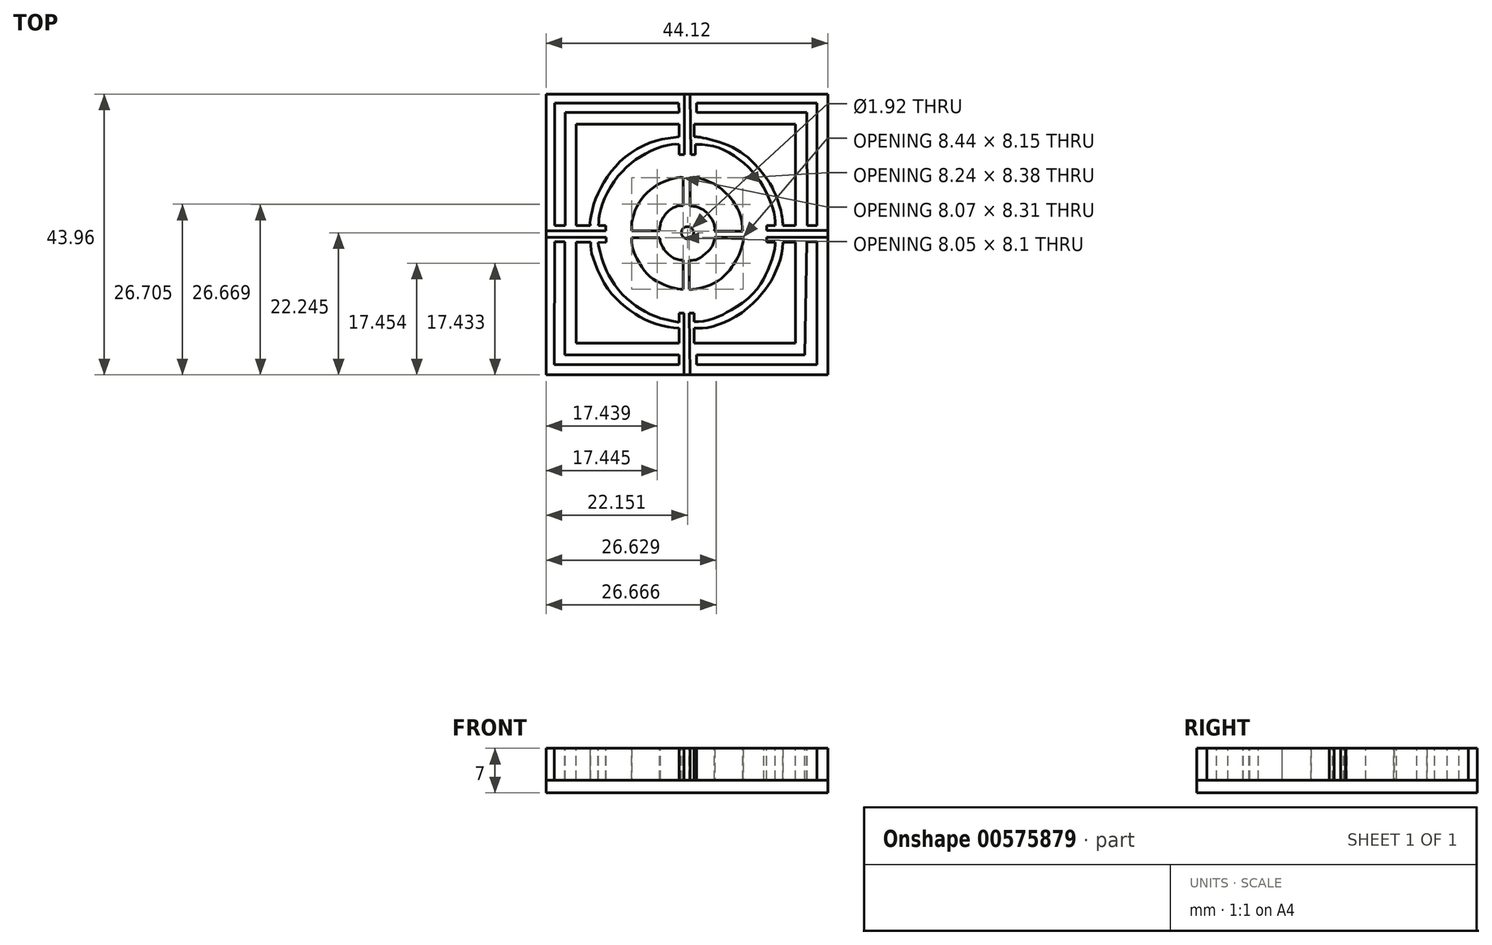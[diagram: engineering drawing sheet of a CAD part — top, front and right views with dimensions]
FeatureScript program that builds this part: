
annotation { "Feature Type Name" : "Feature", "Feature Type Description" : "" }
export const myFeature = defineFeature(function(context is Context, id is Id, definition is map)
    precondition{}
    {
        {
            var Q0;
            Q0=qCreatedBy(makeId("Top.planeOp"),FACE);
            var sketch = newSketch(context, id + "F0", { "sketchPlane" : qUnion([Q0])});
            skFitSpline(sketch, "E0", {"points": [v(14.8, 62.13) * mm, v(14.75, 42.86) * mm], "startDerivative": vector(-0.06, -19.27) * mm, "endDerivative": vector(-0.06, -19.27) * mm});
            skFitSpline(sketch, "E1", {"points": [v(14.75, 42.86) * mm, v(34.31, 42.86) * mm], "startDerivative": vector(19.6, 0) * mm, "endDerivative": vector(19.6, 0) * mm});
            skFitSpline(sketch, "E2", {"points": [v(34.31, 42.86) * mm, v(34.31, 44.38) * mm], "startDerivative": vector(0, 1.53) * mm, "endDerivative": vector(0, 1.53) * mm});
            skFitSpline(sketch, "E3", {"points": [v(34.31, 44.38) * mm, v(16.42, 44.38) * mm], "startDerivative": vector(-17.93, 0) * mm, "endDerivative": vector(-17.93, 0) * mm});
            skFitSpline(sketch, "E4", {"points": [v(16.42, 44.38) * mm, v(16.42, 62.13) * mm], "startDerivative": vector(0, 17.74) * mm, "endDerivative": vector(0, 17.74) * mm});
            skFitSpline(sketch, "E5", {"points": [v(16.42, 62.13) * mm, v(14.8, 62.13) * mm], "startDerivative": vector(-1.62, 0) * mm, "endDerivative": vector(-1.62, 0) * mm});
            skFitSpline(sketch, "E6", {"points": [v(34.31, 50.95) * mm, v(34.31, 46.2) * mm], "startDerivative": vector(0, -4.75) * mm, "endDerivative": vector(0, -4.75) * mm});
            skFitSpline(sketch, "E7", {"points": [v(34.31, 50.95) * mm, v(36.65, 50.95) * mm], "startDerivative": vector(2.34, 0) * mm, "endDerivative": vector(2.34, 0) * mm});
            skFitSpline(sketch, "E8", {"points": [v(36.65, 50.95) * mm, v(36.65, 46.2) * mm], "startDerivative": vector(0, -4.75) * mm, "endDerivative": vector(0, -4.75) * mm});
            skFitSpline(sketch, "E9", {"points": [v(34.31, 49.46) * mm, v(33.12, 49.7) * mm, v(30.97, 50.3) * mm, v(28.74, 51.3) * mm, v(26.75, 52.67) * mm, v(24.79, 54.57) * mm, v(23.3, 56.84) * mm, v(22.67, 58.18) * mm, v(22.03, 60.1) * mm, v(21.6, 62) * mm, v(21.6, 62.01) * mm], "startDerivative": vector(-13.94, 2.4) * mm, "endDerivative": vector(0.26, 5.24) * mm});
            skFitSpline(sketch, "E10", {"points": [v(36.65, 48.6) * mm, v(38.29, 48.6) * mm, v(41.1, 49.37) * mm, v(44.58, 51.33) * mm, v(47.54, 54.27) * mm, v(48.82, 56.2) * mm, v(50.1, 59.12) * mm, v(50.59, 62.01) * mm], "startDerivative": vector(14.49, -1.02) * mm, "endDerivative": vector(1.9, 21.32) * mm});
            skFitSpline(sketch, "E11", {"points": [v(50.59, 62.01) * mm, v(49.36, 62.01) * mm], "startDerivative": vector(-1.25, 0) * mm, "endDerivative": vector(-1.25, 0) * mm});
            skFitSpline(sketch, "E12", {"points": [v(49.36, 62.01) * mm, v(49.36, 61.46) * mm, v(48.89, 59.4) * mm, v(47.94, 57.1) * mm, v(46.93, 55.26) * mm, v(44.59, 52.79) * mm, v(41.9, 51.12) * mm, v(40.57, 50.4) * mm, v(38.37, 49.72) * mm, v(36.65, 49.61) * mm], "startDerivative": vector(0.7, -10.36) * mm, "endDerivative": vector(-15.94, 0) * mm});
            skFitSpline(sketch, "E13", {"points": [v(50.59, 64.63) * mm, v(50.2, 67.1) * mm, v(48.89, 70.6) * mm, v(47.55, 72.58) * mm], "startDerivative": vector(-0.92, 7.67) * mm, "endDerivative": vector(-5.43, 6.35) * mm});
            skFitSpline(sketch, "E14", {"points": [v(47.55, 72.58) * mm, v(46.33, 74.1) * mm, v(42.46, 77) * mm, v(37.58, 78.46) * mm, v(36.87, 78.55) * mm], "startDerivative": vector(-4.95, 6.76) * mm, "endDerivative": vector(-4.27, 0.3) * mm});
            skFitSpline(sketch, "E15", {"points": [v(36.87, 78.55) * mm, v(36.87, 77.33) * mm], "startDerivative": vector(0, -1.08) * mm, "endDerivative": vector(0, -1.08) * mm});
            skFitSpline(sketch, "E16", {"points": [v(36.87, 77.33) * mm, v(37.6, 77.33) * mm, v(39.73, 77.05) * mm, v(42.02, 76.13) * mm, v(44.29, 74.55) * mm, v(46.26, 72.58) * mm, v(47.74, 70.32) * mm, v(48.72, 68.07) * mm, v(49.31, 66.05) * mm, v(49.38, 64.63) * mm], "startDerivative": vector(9.67, 0.58) * mm, "endDerivative": vector(-0.3, -15.03) * mm});
            skFitSpline(sketch, "E17", {"points": [v(49.38, 64.63) * mm, v(50.59, 64.63) * mm], "startDerivative": vector(1.24, 0) * mm, "endDerivative": vector(1.24, 0) * mm});
            skFitSpline(sketch, "E18", {"points": [v(34.3, 77.33) * mm, v(32.9, 77.33) * mm, v(29.97, 76.37) * mm, v(27.17, 74.7) * mm, v(24.52, 72.11) * mm, v(22.5, 68.62) * mm, v(21.8, 66.05) * mm, v(21.69, 64.63) * mm], "startDerivative": vector(-12.77, 1.45) * mm, "endDerivative": vector(-0.42, -12.91) * mm});
            skFitSpline(sketch, "E19", {"points": [v(21.69, 64.63) * mm, v(20.38, 64.63) * mm], "startDerivative": vector(-1.3, 0) * mm, "endDerivative": vector(-1.3, 0) * mm});
            skFitSpline(sketch, "E20", {"points": [v(20.38, 64.63) * mm, v(20.38, 65.43) * mm, v(21.02, 68.16) * mm, v(22.78, 71.84) * mm, v(25.97, 75.45) * mm, v(30.6, 77.89) * mm, v(34.3, 78.55) * mm], "startDerivative": vector(-0.6, 8.43) * mm, "endDerivative": vector(20.4, 2.18) * mm});
            skFitSpline(sketch, "E21", {"points": [v(34.3, 78.55) * mm, v(34.3, 77.33) * mm], "startDerivative": vector(0, -1.08) * mm, "endDerivative": vector(0, -1.08) * mm});
            skFitSpline(sketch, "E22", {"points": [v(22.84, 63.83) * mm, v(22.86, 62.77) * mm], "startDerivative": vector(0.02, -1.07) * mm, "endDerivative": vector(0.02, -1.07) * mm});
            skFitSpline(sketch, "E23", {"points": [v(22.86, 62.77) * mm, v(13.46, 62.77) * mm], "startDerivative": vector(-9.4, 0) * mm, "endDerivative": vector(-9.4, 0) * mm});
            skFitSpline(sketch, "E24", {"points": [v(13.46, 62.77) * mm, v(13.46, 63.83) * mm], "startDerivative": vector(0, 1.07) * mm, "endDerivative": vector(0, 1.07) * mm});
            skFitSpline(sketch, "E25", {"points": [v(13.46, 63.83) * mm, v(22.84, 63.83) * mm], "startDerivative": vector(9.38, 0) * mm, "endDerivative": vector(9.38, 0) * mm});
            skFitSpline(sketch, "E26", {"points": [v(34.93, 52.6) * mm, v(35.87, 52.6) * mm], "startDerivative": vector(0.94, 0) * mm, "endDerivative": vector(0.94, 0) * mm});
            skFitSpline(sketch, "E27", {"points": [v(35.87, 52.6) * mm, v(35.87, 59.23) * mm], "startDerivative": vector(-0.02, 6.18) * mm, "endDerivative": vector(0, 6.62) * mm});
            skFitSpline(sketch, "E28", {"points": [v(34.93, 52.6) * mm, v(34.93, 59.23) * mm], "startDerivative": vector(0, 6.62) * mm, "endDerivative": vector(0, 6.62) * mm});
            skFitSpline(sketch, "E29", {"points": [v(31.17, 62.76) * mm, v(24.72, 62.76) * mm], "startDerivative": vector(-6.45, 0) * mm, "endDerivative": vector(-6.45, 0) * mm});
            skFitSpline(sketch, "E30", {"points": [v(24.72, 62.76) * mm, v(24.72, 63.83) * mm], "startDerivative": vector(0, 1.07) * mm, "endDerivative": vector(0, 1.07) * mm});
            skFitSpline(sketch, "E31", {"points": [v(24.72, 63.83) * mm, v(31.17, 63.83) * mm], "startDerivative": vector(6.45, 0) * mm, "endDerivative": vector(6.45, 0) * mm});
            skFitSpline(sketch, "E32", {"points": [v(34.94, 67.78) * mm, v(34.94, 74.22) * mm], "startDerivative": vector(-0.15, 6.24) * mm, "endDerivative": vector(0, 6.24) * mm});
            skFitSpline(sketch, "E33", {"points": [v(34.94, 74.22) * mm, v(36, 74.22) * mm], "startDerivative": vector(0.93, 0) * mm, "endDerivative": vector(0.93, 0) * mm});
            skFitSpline(sketch, "E34", {"points": [v(36, 74.22) * mm, v(36, 67.78) * mm], "startDerivative": vector(0, -6.44) * mm, "endDerivative": vector(0, -6.44) * mm});
            skCircle(sketch, "E35", {"center": v(35.61, 63.53) * mm, "radius": 0.96 * mm});
            skFitSpline(sketch, "E36", {"points": [v(39.85, 63.76) * mm, v(46.25, 63.76) * mm], "startDerivative": vector(6.42, 0) * mm, "endDerivative": vector(6.42, 0) * mm});
            skFitSpline(sketch, "E37", {"points": [v(46.25, 63.76) * mm, v(46.25, 62.8) * mm], "startDerivative": vector(0, -0.95) * mm, "endDerivative": vector(0, -0.95) * mm});
            skFitSpline(sketch, "E38", {"points": [v(46.25, 62.8) * mm, v(39.85, 62.8) * mm], "startDerivative": vector(-6.42, 0) * mm, "endDerivative": vector(-6.42, 0) * mm});
            skFitSpline(sketch, "E39", {"points": [v(44.3, 62.8) * mm, v(44.3, 62.07) * mm, v(43.78, 60.32) * mm, v(42.9, 58.64) * mm, v(41.5, 56.9) * mm, v(39.16, 55.34) * mm, v(36.44, 54.64) * mm, v(35.87, 54.66) * mm], "startDerivative": vector(0.66, -7) * mm, "endDerivative": vector(-5.02, 2.93) * mm});
            skFitSpline(sketch, "E40", {"points": [v(34.93, 54.66) * mm, v(33.75, 54.81) * mm, v(32.03, 55.34) * mm, v(30.18, 56.31) * mm, v(28.6, 57.96) * mm, v(27.35, 60.14) * mm, v(27.08, 60.97) * mm, v(26.87, 61.97) * mm, v(26.87, 62.76) * mm], "startDerivative": vector(-10.11, 0.86) * mm, "endDerivative": vector(0.5, 8.43) * mm});
            skFitSpline(sketch, "E41", {"points": [v(26.87, 63.83) * mm, v(26.87, 64.85) * mm, v(27.59, 67.38) * mm, v(29.28, 69.79) * mm, v(31.33, 71.28) * mm, v(33.2, 71.95) * mm, v(34.59, 72.2) * mm, v(34.94, 72.14) * mm], "startDerivative": vector(-0.6, 8.13) * mm, "endDerivative": vector(5.04, -1.27) * mm});
            skFitSpline(sketch, "E42", {"points": [v(36, 72.14) * mm, v(37.17, 72.14) * mm, v(38.93, 71.54) * mm, v(40.3, 70.85) * mm, v(41.95, 69.44) * mm, v(43.06, 68.02) * mm, v(43.97, 66.02) * mm, v(44.2, 64.3) * mm, v(44.25, 63.76) * mm], "startDerivative": vector(10.83, 1.07) * mm, "endDerivative": vector(0.71, -6.4) * mm});
            skFitSpline(sketch, "E43", {"points": [v(36.65, 46.2) * mm, v(52.53, 46.2) * mm], "startDerivative": vector(15.86, 0) * mm, "endDerivative": vector(15.86, 0) * mm});
            skFitSpline(sketch, "E44", {"points": [v(52.53, 46.2) * mm, v(52.53, 62.01) * mm], "startDerivative": vector(0, 15.8) * mm, "endDerivative": vector(0, 15.8) * mm});
            skFitSpline(sketch, "E45", {"points": [v(52.53, 62.01) * mm, v(50.59, 62.01) * mm], "startDerivative": vector(-1.96, 0) * mm, "endDerivative": vector(-1.95, 0.01) * mm});
            skFitSpline(sketch, "E46", {"points": [v(52.53, 64.67) * mm, v(50.59, 64.63) * mm], "startDerivative": vector(-1.94, -0.05) * mm, "endDerivative": vector(-1.94, -0.05) * mm});
            skFitSpline(sketch, "E47", {"points": [v(52.53, 64.67) * mm, v(52.53, 80.54) * mm], "startDerivative": vector(0, 15.87) * mm, "endDerivative": vector(0, 15.87) * mm});
            skFitSpline(sketch, "E48", {"points": [v(52.53, 80.54) * mm, v(36.65, 80.54) * mm], "startDerivative": vector(-15.86, 0) * mm, "endDerivative": vector(-15.86, 0) * mm});
            skFitSpline(sketch, "E49", {"points": [v(36.65, 80.54) * mm, v(36.65, 78.55) * mm], "startDerivative": vector(0, -2) * mm, "endDerivative": vector(0, -2) * mm});
            skFitSpline(sketch, "E50", {"points": [v(36.65, 78.55) * mm, v(36.87, 78.55) * mm], "startDerivative": vector(0.18, 0) * mm, "endDerivative": vector(0.18, 0) * mm});
            skFitSpline(sketch, "E51", {"points": [v(34.3, 80.54) * mm, v(34.3, 78.55) * mm], "startDerivative": vector(0, -2) * mm, "endDerivative": vector(0, -2) * mm});
            skFitSpline(sketch, "E52", {"points": [v(34.3, 80.54) * mm, v(18.15, 80.54) * mm], "startDerivative": vector(-16.15, 0) * mm, "endDerivative": vector(-16.15, 0) * mm});
            skFitSpline(sketch, "E53", {"points": [v(18.15, 80.54) * mm, v(18.15, 64.67) * mm], "startDerivative": vector(0, -15.87) * mm, "endDerivative": vector(0, -15.87) * mm});
            skFitSpline(sketch, "E54", {"points": [v(18.15, 64.67) * mm, v(20.38, 64.67) * mm], "startDerivative": vector(2.22, 0) * mm, "endDerivative": vector(2.22, 0) * mm});
            skFitSpline(sketch, "E55", {"points": [v(21.69, 64.63) * mm, v(22.84, 64.63) * mm], "startDerivative": vector(1.15, 0) * mm, "endDerivative": vector(1.15, 0) * mm});
            skFitSpline(sketch, "E56", {"points": [v(22.84, 64.63) * mm, v(22.84, 63.83) * mm], "startDerivative": vector(0, -0.78) * mm, "endDerivative": vector(0, -0.78) * mm});
            skFitSpline(sketch, "E57", {"points": [v(22.86, 62.77) * mm, v(22.86, 62.01) * mm], "startDerivative": vector(0, -0.76) * mm, "endDerivative": vector(0, -0.76) * mm});
            skFitSpline(sketch, "E58", {"points": [v(22.86, 62.01) * mm, v(21.6, 62) * mm], "startDerivative": vector(-1.25, -0.01) * mm, "endDerivative": vector(-1.25, -0.01) * mm});
            skFitSpline(sketch, "E59", {"points": [v(20.49, 62.03) * mm, v(18.15, 62.03) * mm], "startDerivative": vector(-2.38, 0) * mm, "endDerivative": vector(-2.38, 0) * mm});
            skFitSpline(sketch, "E60", {"points": [v(36.87, 77.33) * mm, v(36.87, 75.77) * mm], "startDerivative": vector(0, -1.7) * mm, "endDerivative": vector(0, -1.7) * mm});
            skFitSpline(sketch, "E61", {"points": [v(36.87, 75.77) * mm, v(34.3, 75.77) * mm], "startDerivative": vector(-2.56, 0) * mm, "endDerivative": vector(-2.56, 0) * mm});
            skFitSpline(sketch, "E62", {"points": [v(34.3, 75.77) * mm, v(34.3, 77.33) * mm], "startDerivative": vector(0, 1.7) * mm, "endDerivative": vector(0, 1.7) * mm});
            skFitSpline(sketch, "E63", {"points": [v(49.36, 62.01) * mm, v(48.04, 62.01) * mm], "startDerivative": vector(-1.33, 0) * mm, "endDerivative": vector(-1.33, 0) * mm});
            skFitSpline(sketch, "E64", {"points": [v(48.04, 62.01) * mm, v(48.04, 64.67) * mm], "startDerivative": vector(0, 2.41) * mm, "endDerivative": vector(0, 2.41) * mm});
            skFitSpline(sketch, "E65", {"points": [v(48.04, 64.67) * mm, v(49.38, 64.63) * mm], "startDerivative": vector(1.34, -0.05) * mm, "endDerivative": vector(1.34, -0.05) * mm});
            skFitSpline(sketch, "E66", {"points": [v(18.15, 62.03) * mm, v(18.15, 46.2) * mm], "startDerivative": vector(0, -15.81) * mm, "endDerivative": vector(0, -15.81) * mm});
            skFitSpline(sketch, "E67", {"points": [v(18.15, 46.2) * mm, v(34.31, 46.2) * mm], "startDerivative": vector(16.2, 0) * mm, "endDerivative": vector(16.2, 0) * mm});
            skFitSpline(sketch, "E68", {"points": [v(48.04, 63.87) * mm, v(57.58, 63.87) * mm], "startDerivative": vector(9.55, 0) * mm, "endDerivative": vector(9.55, 0) * mm});
            skFitSpline(sketch, "E69", {"points": [v(57.58, 63.87) * mm, v(57.58, 62.8) * mm], "startDerivative": vector(0, -1.06) * mm, "endDerivative": vector(0, -1.06) * mm});
            skFitSpline(sketch, "E70", {"points": [v(57.58, 62.8) * mm, v(48.04, 62.8) * mm], "startDerivative": vector(-9.55, 0) * mm, "endDerivative": vector(-9.55, 0) * mm});
            skFitSpline(sketch, "E71", {"points": [v(36.16, 75.77) * mm, v(36.02, 85.24) * mm], "startDerivative": vector(-0.15, 9.46) * mm, "endDerivative": vector(-0.15, 9.46) * mm});
            skFitSpline(sketch, "E72", {"points": [v(36.02, 85.24) * mm, v(35.16, 85.24) * mm], "startDerivative": vector(-0.85, 0) * mm, "endDerivative": vector(-0.85, 0) * mm});
            skFitSpline(sketch, "E73", {"points": [v(35.16, 85.24) * mm, v(35.16, 75.77) * mm], "startDerivative": vector(0, -9.46) * mm, "endDerivative": vector(0, -9.46) * mm});
            skFitSpline(sketch, "E74", {"points": [v(37.01, 44.38) * mm, v(37.04, 42.86) * mm], "startDerivative": vector(0.03, -1.53) * mm, "endDerivative": vector(0.03, -1.53) * mm});
            skFitSpline(sketch, "E75", {"points": [v(37.04, 42.86) * mm, v(55.9, 42.86) * mm], "startDerivative": vector(18.85, 0) * mm, "endDerivative": vector(18.85, 0) * mm});
            skFitSpline(sketch, "E76", {"points": [v(55.9, 42.86) * mm, v(55.9, 62.09) * mm], "startDerivative": vector(0, 19.23) * mm, "endDerivative": vector(0, 19.23) * mm});
            skFitSpline(sketch, "E77", {"points": [v(55.9, 62.09) * mm, v(54.34, 62.09) * mm], "startDerivative": vector(-1.56, 0) * mm, "endDerivative": vector(-1.56, 0) * mm});
            skFitSpline(sketch, "E78", {"points": [v(54.34, 62.09) * mm, v(54.02, 44.38) * mm], "startDerivative": vector(-0.32, -17.7) * mm, "endDerivative": vector(-0.32, -17.7) * mm});
            skFitSpline(sketch, "E79", {"points": [v(54.02, 44.38) * mm, v(37.01, 44.38) * mm], "startDerivative": vector(-17, 0) * mm, "endDerivative": vector(-17, 0) * mm});
            skFitSpline(sketch, "E80", {"points": [v(54.4, 64.64) * mm, v(55.89, 64.66) * mm], "startDerivative": vector(1.49, 0.02) * mm, "endDerivative": vector(1.49, 0.02) * mm});
            skFitSpline(sketch, "E81", {"points": [v(55.89, 64.66) * mm, v(55.89, 83.84) * mm], "startDerivative": vector(0, 19.18) * mm, "endDerivative": vector(0, 19.18) * mm});
            skFitSpline(sketch, "E82", {"points": [v(55.89, 83.84) * mm, v(37.02, 83.84) * mm], "startDerivative": vector(-18.87, 0) * mm, "endDerivative": vector(-18.87, 0) * mm});
            skFitSpline(sketch, "E83", {"points": [v(37.02, 83.84) * mm, v(37.02, 82.38) * mm], "startDerivative": vector(0, -1.46) * mm, "endDerivative": vector(0, -1.46) * mm});
            skFitSpline(sketch, "E84", {"points": [v(37.02, 82.38) * mm, v(54.34, 82.38) * mm], "startDerivative": vector(17.31, 0) * mm, "endDerivative": vector(17.31, 0) * mm});
            skFitSpline(sketch, "E85", {"points": [v(54.34, 82.38) * mm, v(54.4, 64.64) * mm], "startDerivative": vector(0.07, -17.74) * mm, "endDerivative": vector(0.07, -17.74) * mm});
            skFitSpline(sketch, "E86", {"points": [v(34.3, 82.38) * mm, v(34.25, 83.84) * mm], "startDerivative": vector(-0.04, 1.46) * mm, "endDerivative": vector(-0.04, 1.46) * mm});
            skFitSpline(sketch, "E87", {"points": [v(34.25, 83.84) * mm, v(14.82, 83.84) * mm], "startDerivative": vector(-19.43, 0) * mm, "endDerivative": vector(-19.43, 0) * mm});
            skFitSpline(sketch, "E88", {"points": [v(14.82, 83.84) * mm, v(14.82, 64.64) * mm], "startDerivative": vector(0, -19.2) * mm, "endDerivative": vector(0, -19.2) * mm});
            skFitSpline(sketch, "E89", {"points": [v(14.82, 64.64) * mm, v(16.48, 64.64) * mm], "startDerivative": vector(1.66, 0) * mm, "endDerivative": vector(1.66, 0) * mm});
            skFitSpline(sketch, "E90", {"points": [v(16.48, 64.64) * mm, v(16.48, 82.38) * mm], "startDerivative": vector(0, 17.74) * mm, "endDerivative": vector(0, 17.74) * mm});
            skFitSpline(sketch, "E91", {"points": [v(16.48, 82.38) * mm, v(34.3, 82.38) * mm], "startDerivative": vector(17.82, 0) * mm, "endDerivative": vector(17.82, 0) * mm});
            skFitSpline(sketch, "E92", {"points": [v(20.49, 62.03) * mm, v(21.6, 62) * mm], "startDerivative": vector(1.07, -0.02) * mm, "endDerivative": vector(1.07, -0.02) * mm});
            skFitSpline(sketch, "E93", {"points": [v(20.49, 62.03) * mm, v(20.49, 60.94) * mm, v(20.87, 59.43) * mm, v(22.36, 56) * mm, v(24.45, 53.2) * mm, v(26.8, 51.22) * mm, v(28.98, 49.93) * mm, v(31.78, 48.92) * mm, v(34.31, 48.55) * mm], "startDerivative": vector(-0.68, -13.26) * mm, "endDerivative": vector(19.93, -1.96) * mm});
            skFitSpline(sketch, "E94", {"points": [v(31.17, 62.76) * mm, v(31.29, 62.76) * mm], "startDerivative": vector(0.11, 0) * mm, "endDerivative": vector(0.11, 0) * mm});
            skFitSpline(sketch, "E95", {"points": [v(31.29, 62.76) * mm, v(31.38, 62.03) * mm, v(32.28, 60.5) * mm, v(33.13, 59.77) * mm, v(33.82, 59.4) * mm, v(34.93, 59.23) * mm], "startDerivative": vector(0, -3.96) * mm, "endDerivative": vector(5.83, -0.46) * mm});
            skFitSpline(sketch, "E96", {"points": [v(31.29, 63.83) * mm, v(31.17, 63.83) * mm], "startDerivative": vector(-0.11, 0) * mm, "endDerivative": vector(-0.11, 0) * mm});
            skFitSpline(sketch, "E97", {"points": [v(31.29, 63.83) * mm, v(31.29, 64.01) * mm, v(31.29, 64.06) * mm], "startDerivative": vector(0, 0.32) * mm, "endDerivative": vector(0, 0.1) * mm});
            skFitSpline(sketch, "E98", {"points": [v(31.29, 64.06) * mm, v(31.29, 64.28) * mm], "startDerivative": vector(0, 0.23) * mm, "endDerivative": vector(0, 0.23) * mm});
            skFitSpline(sketch, "E99", {"points": [v(31.29, 64.28) * mm, v(31.38, 64.84) * mm], "startDerivative": vector(0.1, 0.56) * mm, "endDerivative": vector(0.1, 0.56) * mm});
            skFitSpline(sketch, "E100", {"points": [v(31.38, 64.84) * mm, v(31.49, 65.3) * mm, v(31.95, 66.1) * mm, v(32.63, 66.92) * mm, v(33.5, 67.47) * mm, v(33.88, 67.63) * mm, v(34.4, 67.76) * mm, v(34.94, 67.78) * mm], "startDerivative": vector(0.47, 3.7) * mm, "endDerivative": vector(4.15, 0.31) * mm});
            skFitSpline(sketch, "E101", {"points": [v(35.87, 59.23) * mm, v(36.69, 59.23) * mm, v(37.64, 59.61) * mm, v(38.51, 60.34) * mm, v(39.11, 60.9) * mm, v(39.61, 61.69) * mm, v(39.79, 62.29) * mm, v(39.85, 62.8) * mm], "startDerivative": vector(5.6, -0.46) * mm, "endDerivative": vector(0.2, 4.57) * mm});
            skFitSpline(sketch, "E102", {"points": [v(39.85, 63.76) * mm, v(39.85, 64.68) * mm, v(39.45, 65.62) * mm, v(38.77, 66.48) * mm, v(38.16, 67.05) * mm, v(37.32, 67.46) * mm, v(36.85, 67.61) * mm, v(36.2, 67.69) * mm, v(36, 67.72) * mm, v(36, 67.78) * mm], "startDerivative": vector(0.61, 6.97) * mm, "endDerivative": vector(0.61, 3.18) * mm});
            skFitSpline(sketch, "E103", {"points": [v(35.1, 50.95) * mm, v(35.1, 41.28) * mm], "startDerivative": vector(0, -9.67) * mm, "endDerivative": vector(0, -9.67) * mm});
            skFitSpline(sketch, "E104", {"points": [v(35.87, 50.95) * mm, v(36, 41.28) * mm], "startDerivative": vector(0.12, -9.67) * mm, "endDerivative": vector(0.12, -9.67) * mm});
            skFitSpline(sketch, "E105", {"points": [v(35.1, 41.28) * mm, v(36, 41.28) * mm], "startDerivative": vector(0.9, 0) * mm, "endDerivative": vector(0.9, 0) * mm});
            skSolve(sketch);
        }
        {
            var Q0;
            Q0=makeQuery(id+"F0.imprint","IMPRINT",FACE,{"disambiguationData":[TD([[makeQuery(id+"F0.imprint","IMPRINT",EDGE,{"derivedFrom":sQuery(id+"F0.wireOp",EDGE,"E0")}),1.0]])]});
            var Q1;
            Q1=makeQuery(id+"F0.imprint","IMPRINT",FACE,{"disambiguationData":[TD([[makeQuery(id+"F0.imprint","IMPRINT",EDGE,{"derivedFrom":sQuery(id+"F0.wireOp",EDGE,"E74")}),1.0]])]});
            var Q2;
            Q2=makeQuery(id+"F0.imprint","IMPRINT",FACE,{"disambiguationData":[TD([[makeQuery(id+"F0.imprint","IMPRINT",EDGE,{"derivedFrom":sQuery(id+"F0.wireOp",EDGE,"E80")}),1.0]])]});
            var Q3;
            Q3=makeQuery(id+"F0.imprint","IMPRINT",FACE,{"disambiguationData":[TD([[makeQuery(id+"F0.imprint","IMPRINT",EDGE,{"derivedFrom":sQuery(id+"F0.wireOp",EDGE,"E86")}),1.0]])]});
            var Q4;
            Q4=makeQuery(id+"F0.imprint","IMPRINT",FACE,{"disambiguationData":[TD([[makeQuery(id+"F0.imprint","IMPRINT",EDGE,{"derivedFrom":sQuery(id+"F0.wireOp",EDGE,"E59")}),1.0]])]});
            var Q5;
            Q5=makeQuery(id+"F0.imprint","IMPRINT",FACE,{"disambiguationData":[TD([[makeQuery(id+"F0.imprint","IMPRINT",EDGE,{"derivedFrom":sQuery(id+"F0.wireOp",EDGE,"8e7a7f37-7289-45c1-9748-e4486086e636")}),1.0]])]});
            var Q6;
            {var subQ0=sQuery(id+"F0.wireOp",EDGE,"E43");Q6=makeQuery(id+"F0.imprint","IMPRINT",FACE,{"disambiguationData":[TD([[makeQuery(id+"F0.imprint","IMPRINT",EDGE,{"derivedFrom":subQ0}),1.0]])]});}
            var Q7;
            Q7=makeQuery(id+"F0.imprint","IMPRINT",FACE,{"disambiguationData":[TD([[makeQuery(id+"F0.imprint","IMPRINT",EDGE,{"derivedFrom":sQuery(id+"F0.wireOp",EDGE,"E13")}),-1.0]])]});
            var Q8;
            {var subQ0=sQuery(id+"F0.wireOp",EDGE,"E51");Q8=makeQuery(id+"F0.imprint","IMPRINT",FACE,{"disambiguationData":[TD([[makeQuery(id+"F0.imprint","IMPRINT",EDGE,{"derivedFrom":subQ0}),-1.0]])]});}
            var Q9;
            Q9=makeQuery(id+"F0.imprint","IMPRINT",FACE,{"disambiguationData":[TD([[makeQuery(id+"F0.imprint","IMPRINT",EDGE,{"derivedFrom":sQuery(id+"F0.wireOp",EDGE,"E22")}),-1.0]])]});
            var Q10;
            {var subQ0=sQuery(id+"F0.wireOp",EDGE,"E71");Q10=makeQuery(id+"F0.imprint","IMPRINT",FACE,{"disambiguationData":[TD([[makeQuery(id+"F0.imprint","IMPRINT",EDGE,{"derivedFrom":subQ0}),1.0]])]});}
            var Q11;
            {var subQ0=sQuery(id+"F0.wireOp",EDGE,"E68");Q11=makeQuery(id+"F0.imprint","IMPRINT",FACE,{"disambiguationData":[TD([[makeQuery(id+"F0.imprint","IMPRINT",EDGE,{"derivedFrom":subQ0}),-1.0]])]});}
            var Q12;
            {var subQ7=sQuery(id+"F0.wireOp",EDGE,"E12");Q12=makeQuery(id+"F0.imprint","IMPRINT",FACE,{"disambiguationData":[TD([[makeQuery(id+"F0.imprint","IMPRINT",EDGE,{"derivedFrom":subQ7}),-1.0]])]});}
            var Q13;
            {var subQ15=sQuery(id+"F0.wireOp",EDGE,"E26");Q13=makeQuery(id+"F0.imprint","IMPRINT",FACE,{"disambiguationData":[TD([[makeQuery(id+"F0.imprint","IMPRINT",EDGE,{"derivedFrom":subQ15}),1.0]])]});}
            var Q14;
            {var subQ0=sQuery(id+"F0.wireOp",EDGE,"fad55eca-85ea-4e98-8e92-b1308319f970");Q14=makeQuery(id+"F0.imprint","IMPRINT",FACE,{"disambiguationData":[TD([[makeQuery(id+"F0.imprint","IMPRINT",EDGE,{"derivedFrom":subQ0}),1.0]])]});}
            var Q15;
            {var subQ0=sQuery(id+"F0.wireOp",EDGE,"E103");Q15=makeQuery(id+"F0.imprint","IMPRINT",FACE,{"disambiguationData":[TD([[makeQuery(id+"F0.imprint","IMPRINT",EDGE,{"derivedFrom":subQ0}),1.0]])]});}
            extrude(context, id + "F1", {"entities" : qUnion([Q0, Q1, Q2, Q3, Q4, Q5, Q6, Q7, Q8, Q9, Q10, Q11, Q12, Q13, Q14, Q15]), "oppositeDirection" : true, "depth" : 5 * mm, "offsetDistance" : 25 * mm});
        }
        {
            var Q0;
            Q0=makeQuery(id+"F1.opExtrude","CAP_FACE",FACE,{"disambiguationData":[OSD([sQuery(id+"F0.wireOp",EDGE,"E6"),sQuery(id+"F0.wireOp",EDGE,"E7"),sQuery(id+"F0.wireOp",EDGE,"E8"),sQuery(id+"F0.wireOp",EDGE,"E9"),sQuery(id+"F0.wireOp",EDGE,"E12"),sQuery(id+"F0.wireOp",EDGE,"E16"),sQuery(id+"F0.wireOp",EDGE,"E18"),sQuery(id+"F0.wireOp",EDGE,"E23"),sQuery(id+"F0.wireOp",EDGE,"E24"),sQuery(id+"F0.wireOp",EDGE,"E25"),sQuery(id+"F0.wireOp",EDGE,"E27"),sQuery(id+"F0.wireOp",EDGE,"E28"),sQuery(id+"F0.wireOp",EDGE,"E29"),sQuery(id+"F0.wireOp",EDGE,"E31"),sQuery(id+"F0.wireOp",EDGE,"E32"),sQuery(id+"F0.wireOp",EDGE,"E34"),sQuery(id+"F0.wireOp",EDGE,"E35"),sQuery(id+"F0.wireOp",EDGE,"E36"),sQuery(id+"F0.wireOp",EDGE,"E38"),sQuery(id+"F0.wireOp",EDGE,"E39"),sQuery(id+"F0.wireOp",EDGE,"E40"),sQuery(id+"F0.wireOp",EDGE,"E41"),sQuery(id+"F0.wireOp",EDGE,"E42"),sQuery(id+"F0.wireOp",EDGE,"E55"),sQuery(id+"F0.wireOp",EDGE,"E56"),sQuery(id+"F0.wireOp",EDGE,"E57"),sQuery(id+"F0.wireOp",EDGE,"E58"),sQuery(id+"F0.wireOp",EDGE,"E60"),sQuery(id+"F0.wireOp",EDGE,"E61"),sQuery(id+"F0.wireOp",EDGE,"E62"),sQuery(id+"F0.wireOp",EDGE,"E63"),sQuery(id+"F0.wireOp",EDGE,"E64"),sQuery(id+"F0.wireOp",EDGE,"E65"),sQuery(id+"F0.wireOp",EDGE,"E68"),sQuery(id+"F0.wireOp",EDGE,"E69"),sQuery(id+"F0.wireOp",EDGE,"E70"),sQuery(id+"F0.wireOp",EDGE,"E71"),sQuery(id+"F0.wireOp",EDGE,"E72"),sQuery(id+"F0.wireOp",EDGE,"E73"),sQuery(id+"F0.wireOp",EDGE,"E94"),sQuery(id+"F0.wireOp",EDGE,"E95"),sQuery(id+"F0.wireOp",EDGE,"E96"),sQuery(id+"F0.wireOp",EDGE,"E97"),sQuery(id+"F0.wireOp",EDGE,"E98"),sQuery(id+"F0.wireOp",EDGE,"E99"),sQuery(id+"F0.wireOp",EDGE,"E100"),sQuery(id+"F0.wireOp",EDGE,"E101"),sQuery(id+"F0.wireOp",EDGE,"E102"),sQuery(id+"F0.wireOp",EDGE,"E103"),sQuery(id+"F0.wireOp",EDGE,"E104"),sQuery(id+"F0.wireOp",EDGE,"E105")])],"isStart":false});
            var sketch = newSketch(context, id + "F2", { "sketchPlane" : qUnion([Q0])});
            skLineSegment(sketch, "E106", {"start": v(36, -41.28) * mm, "end": v(57.58, -41.28) * mm});
            skLineSegment(sketch, "E107", {"start": v(57.58, -41.28) * mm, "end": v(35.1, -41.28) * mm});
            skLineSegment(sketch, "E108", {"start": v(35.1, -41.28) * mm, "end": v(13.46, -41.28) * mm});
            skLineSegment(sketch, "E109", {"start": v(13.46, -41.28) * mm, "end": v(13.46, -85.24) * mm});
            skLineSegment(sketch, "E110", {"start": v(13.46, -85.24) * mm, "end": v(57.58, -85.24) * mm});
            skLineSegment(sketch, "E111", {"start": v(57.58, -85.24) * mm, "end": v(57.58, -41.28) * mm});
            skSolve(sketch);
        }
        {
            var Q0;
            Q0 = qSketchRegion(id + "F2", true);
            extrude(context, id + "F3", {"entities" : qUnion([Q0]), "depth" : 2 * mm, "offsetDistance" : 25 * mm});
        }
    });
